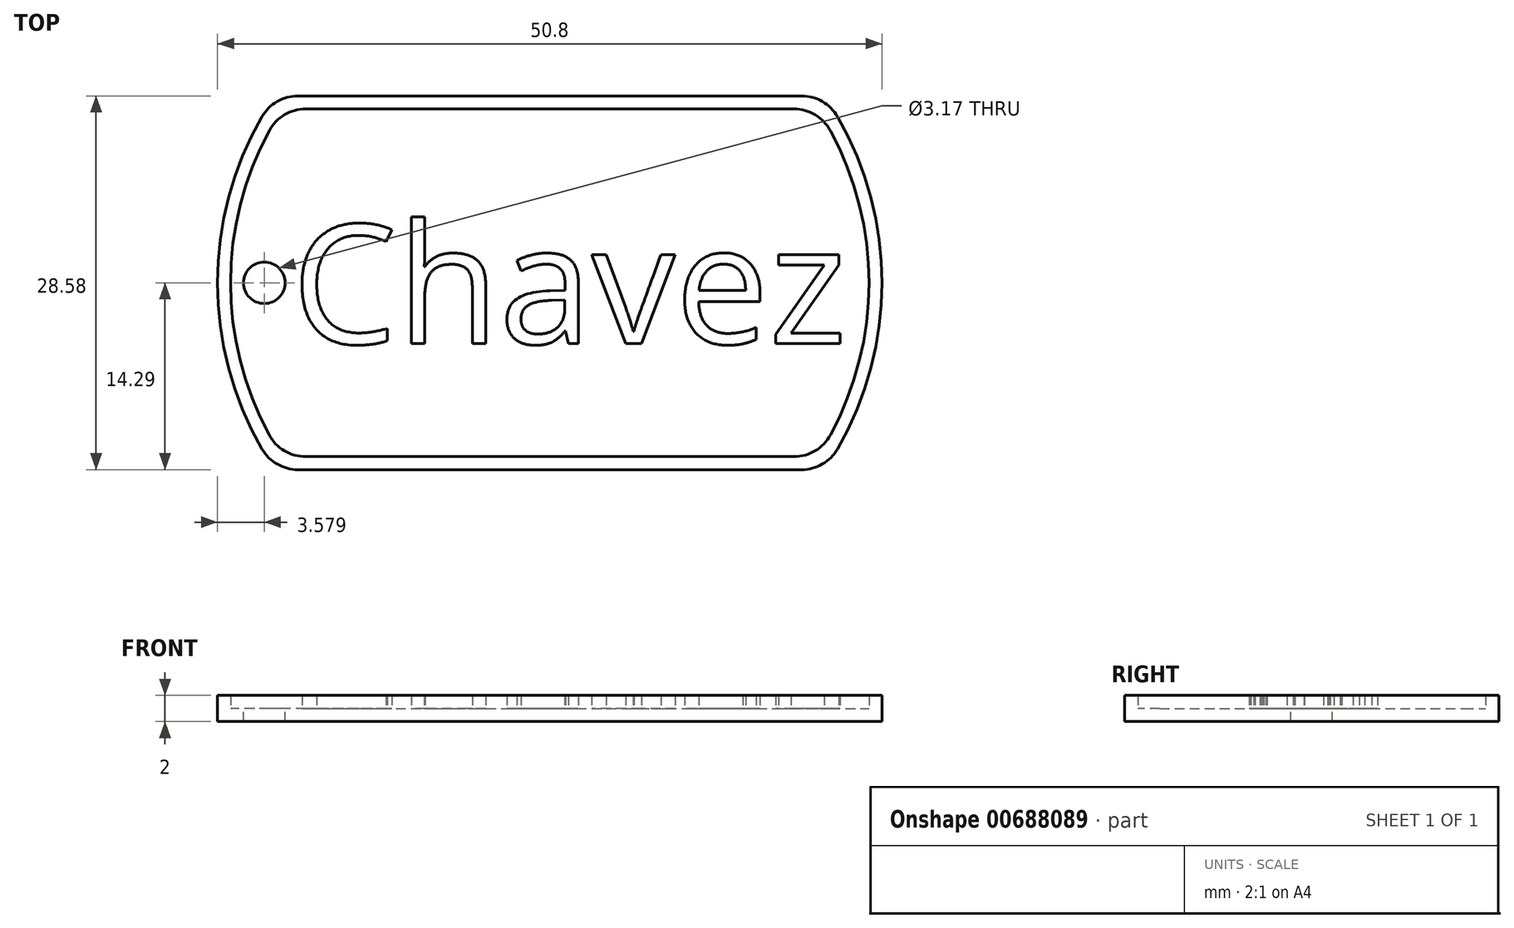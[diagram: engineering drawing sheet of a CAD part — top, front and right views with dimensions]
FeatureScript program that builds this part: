
annotation { "Feature Type Name" : "Feature", "Feature Type Description" : "" }
export const myFeature = defineFeature(function(context is Context, id is Id, definition is map)
    precondition{}
    {
        {
            var Q0;
            Q0=qCreatedBy(makeId("Top.planeOp"),FACE);
            var sketch = newSketch(context, id + "F0", { "sketchPlane" : qUnion([Q0])});
            skArc(sketch, "E0", {"start": v(-22, 12.7) * mm, "mid": v(-25.4, 0) * mm, "end": v(-22, -12.7) * mm});
            skLineSegment(sketch, "E1.top", {"start": v(-19.25, -14.29) * mm, "end": v(19.25, -14.29) * mm});
            skArc(sketch, "E2.trimOffspring", {"start": v(22, -12.7) * mm, "mid": v(25.4, 0) * mm, "end": v(22, 12.7) * mm});
            skLineSegment(sketch, "E3", {"start": v(-19.25, 14.29) * mm, "end": v(19.25, 14.29) * mm});
            skPoint(sketch, "E4.visualSharp", {"position": v(-21, 14.29) * mm});
            skArc(sketch, "E4.filletArc", {"start": v(-19.25, 14.29) * mm, "mid": v(-20.83, 13.86) * mm, "end": v(-22, 12.7) * mm});
            skPoint(sketch, "E5.visualSharp", {"position": v(21, 14.29) * mm});
            skArc(sketch, "E5.filletArc", {"start": v(22, 12.7) * mm, "mid": v(20.83, 13.86) * mm, "end": v(19.25, 14.29) * mm});
            skPoint(sketch, "E6.visualSharp", {"position": v(21, -14.29) * mm});
            skArc(sketch, "E6.filletArc", {"start": v(19.25, -14.29) * mm, "mid": v(20.83, -13.86) * mm, "end": v(22, -12.7) * mm});
            skPoint(sketch, "E7.visualSharp", {"position": v(-21, -14.29) * mm});
            skArc(sketch, "E7.filletArc", {"start": v(-22, -12.7) * mm, "mid": v(-20.83, -13.86) * mm, "end": v(-19.25, -14.29) * mm});
            skSolve(sketch);
        }
        {
            var Q0;
            Q0=makeQuery(id+"F0.imprint","IMPRINT",FACE,{"disambiguationData":[TD([[makeQuery(id+"F0.imprint","IMPRINT",EDGE,{"derivedFrom":sQuery(id+"F0.wireOp",EDGE,"E0")}),1.0]])]});
            extrude(context, id + "F1", {"entities" : qUnion([Q0]), "depth" : 1 * mm, "offsetDistance" : 25.4 * mm});
        }
        {
            var Q0;
            Q0=makeQuery(id+"F1.opExtrude","CAP_FACE",FACE,{"disambiguationData":[OSD([sQuery(id+"F0.wireOp",EDGE,"E0"),sQuery(id+"F0.wireOp",EDGE,"E1.top"),sQuery(id+"F0.wireOp",EDGE,"E2.trimOffspring"),sQuery(id+"F0.wireOp",EDGE,"E3"),sQuery(id+"F0.wireOp",EDGE,"E4.filletArc"),sQuery(id+"F0.wireOp",EDGE,"E5.filletArc"),sQuery(id+"F0.wireOp",EDGE,"E6.filletArc"),sQuery(id+"F0.wireOp",EDGE,"E7.filletArc")])],"isStart":false});
            var sketch = newSketch(context, id + "F2", { "sketchPlane" : qUnion([Q0])});
            skLineSegment(sketch, "E8.0", {"start": v(-18.66, 13.29) * mm, "end": v(18.66, 13.29) * mm});
            skArc(sketch, "E8.1", {"start": v(-21.45, 11.63) * mm, "mid": v(-24.4, 0) * mm, "end": v(-21.45, -11.63) * mm});
            skLineSegment(sketch, "E8.2", {"start": v(-18.66, -13.29) * mm, "end": v(18.66, -13.29) * mm});
            skArc(sketch, "E8.3", {"start": v(21.45, -11.63) * mm, "mid": v(24.4, 0) * mm, "end": v(21.45, 11.63) * mm});
            skPoint(sketch, "E9.visualSharp", {"position": v(-20.46, 13.29) * mm});
            skArc(sketch, "E9.filletArc", {"start": v(-18.66, 13.29) * mm, "mid": v(-20.29, 12.84) * mm, "end": v(-21.45, 11.63) * mm});
            skPoint(sketch, "E10.visualSharp", {"position": v(20.46, 13.29) * mm});
            skArc(sketch, "E10.filletArc", {"start": v(21.45, 11.63) * mm, "mid": v(20.29, 12.84) * mm, "end": v(18.66, 13.29) * mm});
            skPoint(sketch, "E11.visualSharp", {"position": v(20.46, -13.29) * mm});
            skArc(sketch, "E11.filletArc", {"start": v(18.66, -13.29) * mm, "mid": v(20.29, -12.84) * mm, "end": v(21.45, -11.63) * mm});
            skPoint(sketch, "E12.visualSharp", {"position": v(-20.46, -13.29) * mm});
            skArc(sketch, "E12.filletArc", {"start": v(-21.45, -11.63) * mm, "mid": v(-20.29, -12.84) * mm, "end": v(-18.66, -13.29) * mm});
            skLineSegment(sketch, "E13.0", {"start": v(-19.25, 14.29) * mm, "end": v(19.25, 14.29) * mm});
            skArc(sketch, "E13.1", {"start": v(-22, 12.7) * mm, "mid": v(-25.4, 0) * mm, "end": v(-22, -12.7) * mm});
            skLineSegment(sketch, "E13.2", {"start": v(-19.25, -14.29) * mm, "end": v(19.25, -14.29) * mm});
            skArc(sketch, "E13.3", {"start": v(22, -12.7) * mm, "mid": v(25.4, 0) * mm, "end": v(22, 12.7) * mm});
            skPoint(sketch, "E14.visualSharp", {"position": v(-21, -14.29) * mm});
            skArc(sketch, "E14.filletArc", {"start": v(-22, -12.7) * mm, "mid": v(-20.83, -13.86) * mm, "end": v(-19.25, -14.29) * mm});
            skPoint(sketch, "E15.visualSharp", {"position": v(21, -14.29) * mm});
            skArc(sketch, "E15.filletArc", {"start": v(19.25, -14.29) * mm, "mid": v(20.83, -13.86) * mm, "end": v(22, -12.7) * mm});
            skPoint(sketch, "E16.visualSharp", {"position": v(21, 14.29) * mm});
            skArc(sketch, "E16.filletArc", {"start": v(22, 12.7) * mm, "mid": v(20.83, 13.86) * mm, "end": v(19.25, 14.29) * mm});
            skPoint(sketch, "E17.visualSharp", {"position": v(-21, 14.29) * mm});
            skArc(sketch, "E17.filletArc", {"start": v(-19.25, 14.29) * mm, "mid": v(-20.83, 13.86) * mm, "end": v(-22, 12.7) * mm});
            skSolve(sketch);
        }
        {
            var Q0;
            Q0=makeQuery(id+"F2.imprint","IMPRINT",FACE,{"disambiguationData":[TD([[makeQuery(id+"F2.imprint","IMPRINT",EDGE,{"derivedFrom":sQuery(id+"F2.wireOp",EDGE,"E8.0")}),1.0]])]});
            extrude(context, id + "F3", {"entities" : qUnion([Q0]), "operationType" : NewBodyOperationType.ADD, "depth" : 1 * mm, "offsetDistance" : 25.4 * mm});
        }
        {
            var Q0;
            Q0=makeQuery(id+"F1.opExtrude","CAP_FACE",FACE,{"disambiguationData":[OSD([sQuery(id+"F0.wireOp",EDGE,"E0"),sQuery(id+"F0.wireOp",EDGE,"E1.top"),sQuery(id+"F0.wireOp",EDGE,"E2.trimOffspring"),sQuery(id+"F0.wireOp",EDGE,"E3"),sQuery(id+"F0.wireOp",EDGE,"E4.filletArc"),sQuery(id+"F0.wireOp",EDGE,"E5.filletArc"),sQuery(id+"F0.wireOp",EDGE,"E6.filletArc"),sQuery(id+"F0.wireOp",EDGE,"E7.filletArc")])],"isStart":false});
            var sketch = newSketch(context, id + "F4", { "sketchPlane" : qUnion([Q0])});
            skCircle(sketch, "E18", {"center": v(-21.82, 0) * mm, "radius": 1.59 * mm});
            skSolve(sketch);
        }
        {
            var Q0;
            Q0=makeQuery(id+"F4.imprint","IMPRINT",FACE,{"disambiguationData":[TD([[makeQuery(id+"F4.imprint","IMPRINT",EDGE,{"derivedFrom":sQuery(id+"F4.wireOp",EDGE,"E18")}),1.0]])]});
            extrude(context, id + "F5", {"entities" : qUnion([Q0]), "operationType" : NewBodyOperationType.REMOVE, "oppositeDirection" : true, "depth" : 1 * mm, "offsetDistance" : 25.4 * mm});
        }
        {
            var Q0;
            Q0=makeQuery(id+"F2.imprint","IMPRINT",FACE,{"disambiguationData":[TD([[makeQuery(id+"F2.imprint","IMPRINT",EDGE,{"derivedFrom":sQuery(id+"F2.wireOp",EDGE,"E8.0")}),-1.0]])]});
            var sketch = newSketch(context, id + "F6", { "sketchPlane" : qUnion([Q0])});
            skText(sketch, "E19", { "text": "Chavez", "fontName": "OpenSans-Regular.ttf"});
            const initialGuessF6  = {"E19": [-0.01972, -0.00465, 1, 0, 0.00917]};
            skSetInitialGuess(sketch, initialGuessF6);
            skSolve(sketch);
        }
        {
            var Q0;
            Q0 = qSketchRegion(id + "F6", true);
            extrude(context, id + "F7", {"entities" : qUnion([Q0]), "operationType" : NewBodyOperationType.ADD, "depth" : 1 * mm, "offsetDistance" : 25.4 * mm});
        }
    });
